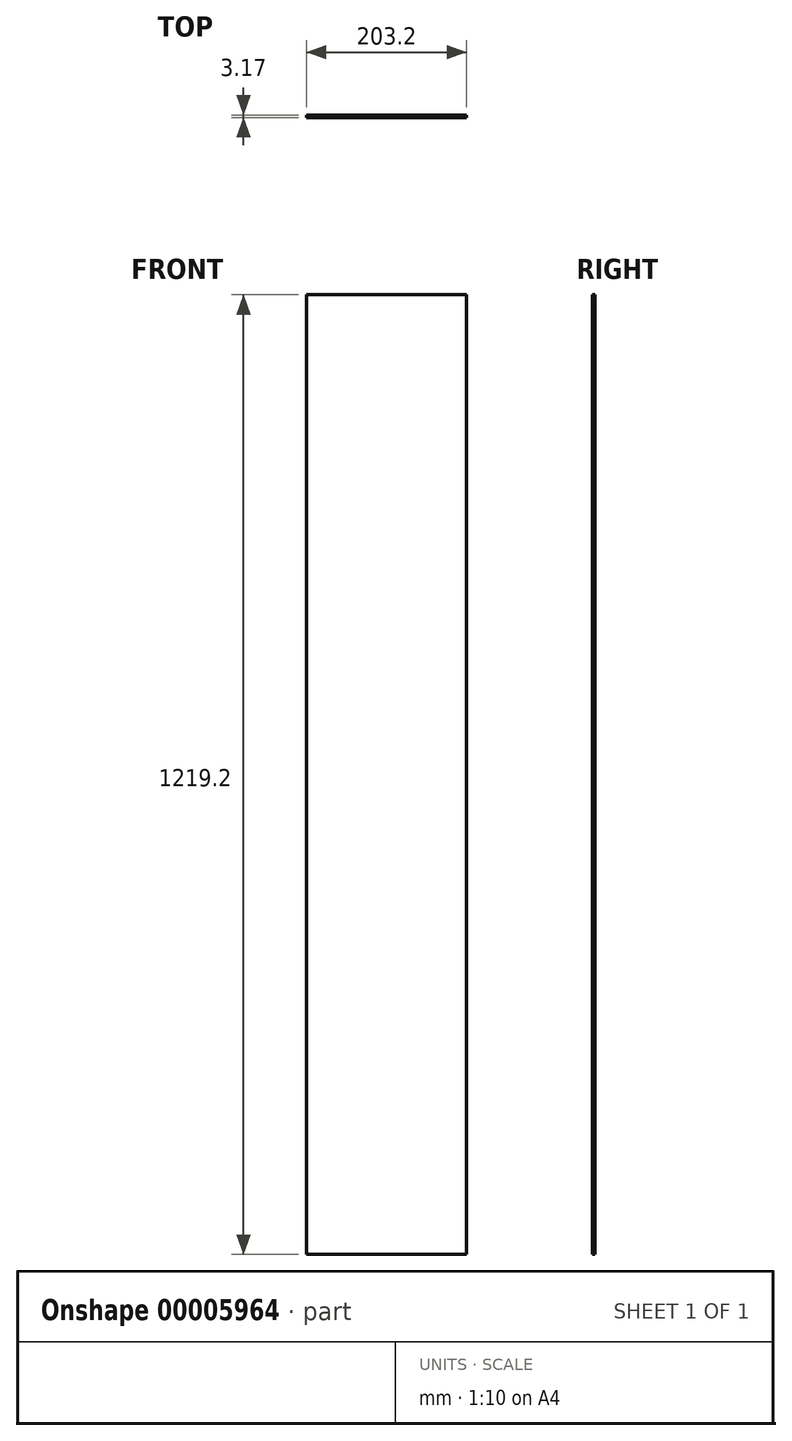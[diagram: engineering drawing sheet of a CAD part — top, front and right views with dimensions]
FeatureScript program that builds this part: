
annotation { "Feature Type Name" : "Feature", "Feature Type Description" : "" }
export const myFeature = defineFeature(function(context is Context, id is Id, definition is map)
    precondition{}
    {
        {
            var Q0;
            Q0=qCreatedBy(makeId("Front.planeOp"),FACE);
            var sketch = newSketch(context, id + "F0", { "sketchPlane" : qUnion([Q0])});
            skLineSegment(sketch, "E0.bottom", {"start": v(-424.22, 536.33) * mm, "end": v(-221.02, 536.33) * mm});
            skLineSegment(sketch, "E0.top", {"start": v(-424.22, -682.87) * mm, "end": v(-221.02, -682.87) * mm});
            skLineSegment(sketch, "E0.left", {"start": v(-424.22, 536.33) * mm, "end": v(-424.22, -682.87) * mm});
            skLineSegment(sketch, "E0.right", {"start": v(-221.02, 536.33) * mm, "end": v(-221.02, -682.87) * mm});
            skSolve(sketch);
        }
        {
            var Q0;
            Q0=qSketchRegion(id+"F0",true);
            extrude(context, id + "F1", {"entities" : qUnion([Q0]), "depth" : 3.17 * mm});
        }
    });
